# Revit family: AM 950 F HH
name_source: partatom
category: Mechanical Equipment
units: mm (PartAtom-declared; Revit-internal decimal feet)

## family parameters
Always vertical = Yes
Cut with Voids When Loaded = No
OmniClass Number = 23.75.00.00
OmniClass Title = Climate Control (HVAC)
Part Type = Normal
Room Calculation Point = No
Round Connector Dimension = Use Diameter
Shared = No
Work Plane-Based = No

## types (1)
- AM 950 F HH
    BMS IN = (PTS) 2x2x0,6
    BMS Out = (PTS) 2x2x0,6
    BMS Panel = (PTS) 2x2x0,6
    Condensate = 9 mm  [stored 0.0295276 ft]
    Condensate conector = Ø6/9 mm
    Electrical connection = 220-240V/50Hz, ~1N+PE or 220-240V/50Hz, ~3N+PE
    Exhaust Air = 315 mm
    Manufacturer = Airmaster A/S
    Max. flow rate 30 dB(A) with ePM10 50% filters = 730 m³
    Max. flow rate 30 dB(A) with ePM10 55% filters = 715 m³
    Max. flow rate 35 dB(A) with ePM10 50% filters = 915 m³
    Max. flow rate 35 dB(A) with ePM10 55% filters = 912 m³
    Maximum current, air handling unit = 2.76 A
    Model = AM 950 F HH
    Network Conection = AWG 24 CAT 5e STP
    Nominal current, electrical comfort heating surface = 7,39 A
    Nominal current, electrical preheating surface = 10,0 A
    Publication date = 16.06.2025
    Suply Air In = 315 mm
    Total Depth = 660 mm
    Total Hight = 2121 mm
    Total Width = 1150 mm  [stored 3.77297 ft]
    URL = www.airmaster-as.com
    Version = 1.0
    Water Heater Surface IN = 15 mm  [stored 0.0492126 ft]
    Water Heater Surface Return = 15 mm  [stored 0.0492126 ft]
    Weight (Standard Unit) = 301.5

note: [stored X ft] marks values corroborated as IEEE doubles in the binary element streams (Revit-internal decimal feet)

## geometry (parser evidence)
native form markers: Sweep x4
no freeform markers — native parametric forms only
